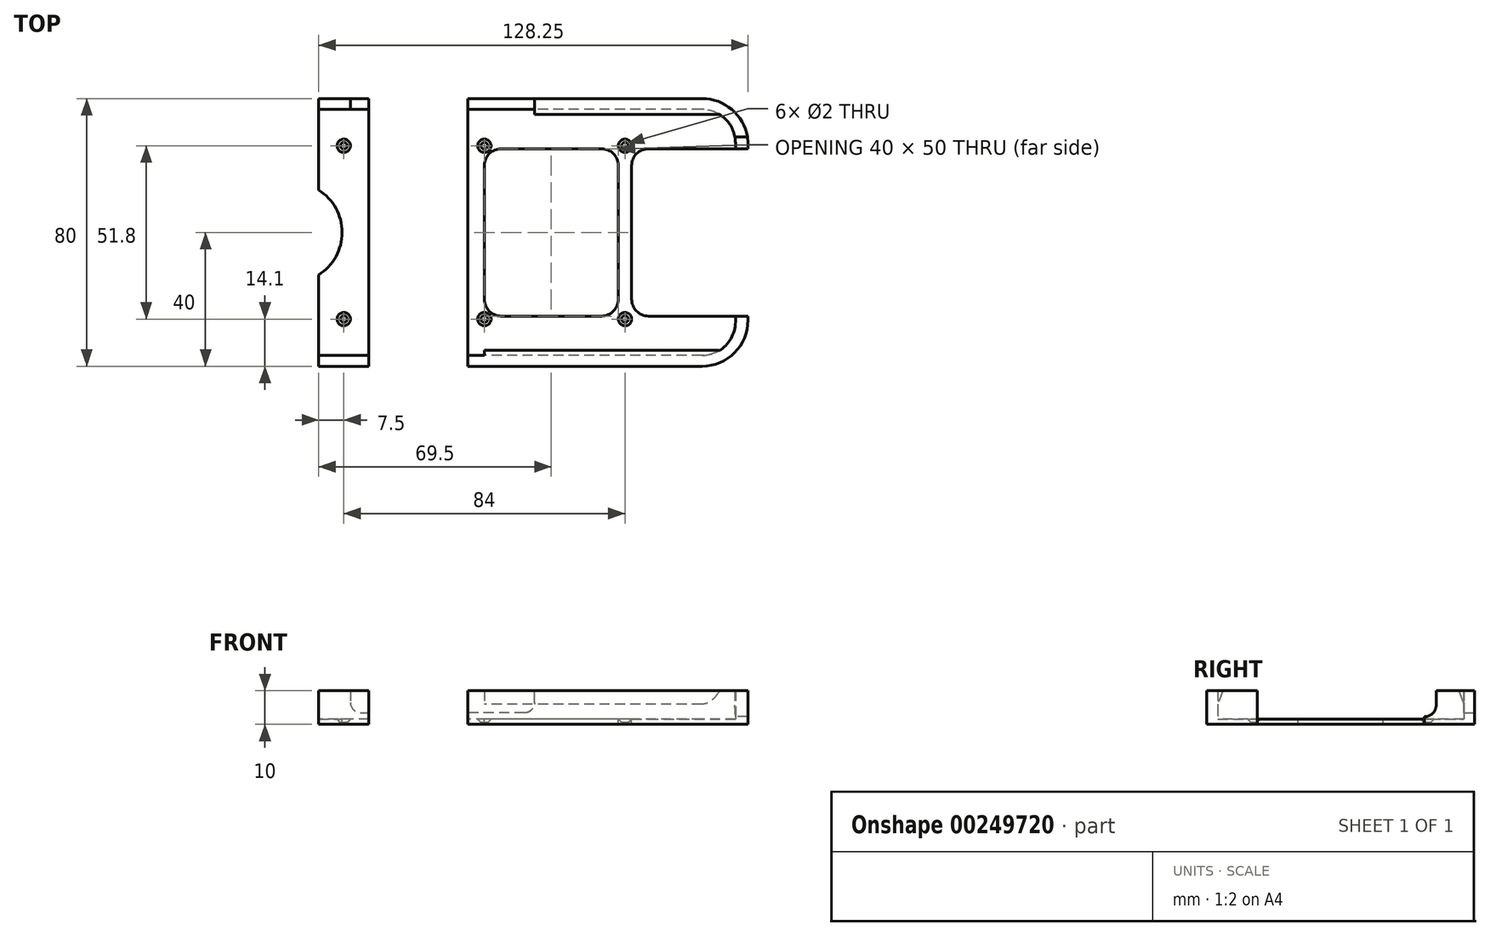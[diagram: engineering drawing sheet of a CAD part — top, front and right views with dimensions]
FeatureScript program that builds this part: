
annotation { "Feature Type Name" : "Feature", "Feature Type Description" : "" }
export const myFeature = defineFeature(function(context is Context, id is Id, definition is map)
    precondition{}
    {
        {
            var Q0;
            Q0=qCreatedBy(makeId("Top.planeOp"),FACE);
            var sketch = newSketch(context, id + "F0", { "sketchPlane" : qUnion([Q0])});
            skCircle(sketch, "E0", {"center": v(0, 25.9) * mm, "radius": 1 * mm});
            skCircle(sketch, "E1", {"center": v(0, -25.9) * mm, "radius": 1 * mm});
            skLineSegment(sketch, "E2", {"start": v(0, 25.9) * mm, "end": v(0, -25.9) * mm, "construction": true});
            skCircle(sketch, "E3", {"center": v(-42, 25.9) * mm, "radius": 1 * mm});
            skCircle(sketch, "E4", {"center": v(42, 25.9) * mm, "radius": 1 * mm});
            skLineSegment(sketch, "E5", {"start": v(-42, 25.9) * mm, "end": v(42, 25.9) * mm, "construction": true});
            skCircle(sketch, "E6.MirrorC", {"center": v(-42, -25.9) * mm, "radius": 1 * mm});
            skCircle(sketch, "E7.MirrorC", {"center": v(42, -25.9) * mm, "radius": 1 * mm});
            skLineSegment(sketch, "E8", {"start": v(75, 26.75) * mm, "end": v(75, -26.75) * mm});
            skPoint(sketch, "E9.middle", {"position": v(0, 0) * mm});
            skPoint(sketch, "E10", {"position": v(75, 0) * mm});
            skLineSegment(sketch, "E11", {"start": v(65, 36.75) * mm, "end": v(0, 36.75) * mm});
            skLineSegment(sketch, "E12", {"start": v(65, -36.75) * mm, "end": v(0, -36.75) * mm});
            skPoint(sketch, "E13.visualSharp", {"position": v(75, 36.75) * mm});
            skArc(sketch, "E13.filletArc", {"start": v(75, 26.75) * mm, "mid": v(72.07, 33.82) * mm, "end": v(65, 36.75) * mm});
            skPoint(sketch, "E14.visualSharp", {"position": v(75, -36.75) * mm});
            skArc(sketch, "E14.filletArc", {"start": v(65, -36.75) * mm, "mid": v(72.07, -33.82) * mm, "end": v(75, -26.75) * mm});
            skLineSegment(sketch, "E15", {"start": v(-5, 40) * mm, "end": v(-5, -40) * mm});
            skPoint(sketch, "E16", {"position": v(-5, 0) * mm});
            skLineSegment(sketch, "E17", {"start": v(0, 36.75) * mm, "end": v(-5, 36.75) * mm});
            skLineSegment(sketch, "E18", {"start": v(0, -36.75) * mm, "end": v(-5, -36.75) * mm});
            skLineSegment(sketch, "E19", {"start": v(-5, 40) * mm, "end": v(65, 40) * mm});
            skLineSegment(sketch, "E20", {"start": v(-5, -40) * mm, "end": v(65, -40) * mm});
            skLineSegment(sketch, "E21", {"start": v(78.75, 26.25) * mm, "end": v(78.75, -26.25) * mm});
            skPoint(sketch, "E22.visualSharp", {"position": v(78.75, 40) * mm});
            skArc(sketch, "E22.filletArc", {"start": v(78.75, 26.25) * mm, "mid": v(74.72, 35.97) * mm, "end": v(65, 40) * mm});
            skPoint(sketch, "E23.visualSharp", {"position": v(78.75, -40) * mm});
            skArc(sketch, "E23.filletArc", {"start": v(65, -40) * mm, "mid": v(74.72, -35.97) * mm, "end": v(78.75, -26.25) * mm});
            skLineSegment(sketch, "E24", {"start": v(25, 36.75) * mm, "end": v(25, 40) * mm});
            skLineSegment(sketch, "E25.MirrorCS", {"start": v(25, -36.75) * mm, "end": v(25, -40) * mm});
            skLineSegment(sketch, "E26", {"start": v(75, 25) * mm, "end": v(78.75, 25) * mm});
            skLineSegment(sketch, "E27", {"start": v(75, -25) * mm, "end": v(78.75, -25) * mm});
            skLineSegment(sketch, "E28", {"start": v(-42, 25.9) * mm, "end": v(-42, -25.9) * mm, "construction": true});
            skLineSegment(sketch, "E29.bottom", {"start": v(-34.5, -40) * mm, "end": v(-49.5, -40) * mm});
            skLineSegment(sketch, "E29.top", {"start": v(-34.5, 40) * mm, "end": v(-49.5, 40) * mm});
            skLineSegment(sketch, "E29.left", {"start": v(-34.5, -40) * mm, "end": v(-34.5, 40) * mm});
            skLineSegment(sketch, "E29.right", {"start": v(-49.5, -40) * mm, "end": v(-49.5, 40) * mm});
            skPoint(sketch, "E29.middle", {"position": v(-42, 0) * mm});
            skLineSegment(sketch, "E30", {"start": v(-34.5, 36.75) * mm, "end": v(-49.5, 36.75) * mm});
            skLineSegment(sketch, "E31", {"start": v(-34.5, -36.75) * mm, "end": v(-49.5, -36.75) * mm});
            skArc(sketch, "E32", {"start": v(-49.5, 12.69) * mm, "mid": v(-42.5, 0) * mm, "end": v(-49.5, -12.69) * mm});
            skLineSegment(sketch, "E33", {"start": v(75, 25) * mm, "end": v(49, 25) * mm});
            skLineSegment(sketch, "E34", {"start": v(44, 20) * mm, "end": v(44, -20) * mm});
            skLineSegment(sketch, "E35", {"start": v(49, -25) * mm, "end": v(75, -25) * mm});
            skPoint(sketch, "E36", {"position": v(44, 0) * mm});
            skLineSegment(sketch, "E37.bottom", {"start": v(35, -25) * mm, "end": v(5, -25) * mm});
            skLineSegment(sketch, "E37.top", {"start": v(35, 25) * mm, "end": v(5, 25) * mm});
            skLineSegment(sketch, "E37.left", {"start": v(40, -20) * mm, "end": v(40, 20) * mm});
            skLineSegment(sketch, "E37.right", {"start": v(0, -20) * mm, "end": v(0, 20) * mm});
            skPoint(sketch, "E37.middle", {"position": v(20, 0) * mm});
            skPoint(sketch, "E38.visualSharp", {"position": v(0, 25) * mm});
            skArc(sketch, "E38.filletArc", {"start": v(5, 25) * mm, "mid": v(1.46, 23.54) * mm, "end": v(0, 20) * mm});
            skPoint(sketch, "E39.visualSharp", {"position": v(40, 25) * mm});
            skArc(sketch, "E39.filletArc", {"start": v(40, 20) * mm, "mid": v(38.54, 23.54) * mm, "end": v(35, 25) * mm});
            skPoint(sketch, "E40.visualSharp", {"position": v(44, 25) * mm});
            skArc(sketch, "E40.filletArc", {"start": v(49, 25) * mm, "mid": v(45.46, 23.54) * mm, "end": v(44, 20) * mm});
            skPoint(sketch, "E41.visualSharp", {"position": v(0, -25) * mm});
            skArc(sketch, "E41.filletArc", {"start": v(0, -20) * mm, "mid": v(1.46, -23.54) * mm, "end": v(5, -25) * mm});
            skPoint(sketch, "E42.visualSharp", {"position": v(40, -25) * mm});
            skArc(sketch, "E42.filletArc", {"start": v(35, -25) * mm, "mid": v(38.54, -23.54) * mm, "end": v(40, -20) * mm});
            skPoint(sketch, "E43.visualSharp", {"position": v(44, -25) * mm});
            skArc(sketch, "E43.filletArc", {"start": v(44, -20) * mm, "mid": v(45.46, -23.54) * mm, "end": v(49, -25) * mm});
            skSolve(sketch);
        }
        {
            var Q0;
            Q0=makeQuery(id+"F0.imprint","IMPRINT",FACE,{"disambiguationData":[TD([[makeQuery(id+"F0.imprint","IMPRINT",EDGE,{"derivedFrom":sQuery(id+"F0.wireOp",EDGE,"E0")}),-1.0]])]});
            var Q1;
            Q1=makeQuery(id+"F0.imprint","IMPRINT",FACE,{"disambiguationData":[TD([[makeQuery(id+"F0.imprint","IMPRINT",EDGE,{"derivedFrom":sQuery(id+"F0.wireOp",EDGE,"E3")}),-1.0]])]});
            var Q2;
            {var subQ0=sQuery(id+"F0.wireOp",EDGE,"E29.top");Q2=makeQuery(id+"F0.imprint","IMPRINT",FACE,{"disambiguationData":[TD([[makeQuery(id+"F0.imprint","IMPRINT",EDGE,{"derivedFrom":subQ0}),1.0]])]});}
            var Q3;
            {var subQ4=sQuery(id+"F0.wireOp",EDGE,"E17");Q3=makeQuery(id+"F0.imprint","IMPRINT",FACE,{"disambiguationData":[TD([[makeQuery(id+"F0.imprint","IMPRINT",EDGE,{"derivedFrom":subQ4}),-1.0]])]});}
            var Q4;
            {var subQ0=sQuery(id+"F0.wireOp",EDGE,"E29.bottom");Q4=makeQuery(id+"F0.imprint","IMPRINT",FACE,{"disambiguationData":[TD([[makeQuery(id+"F0.imprint","IMPRINT",EDGE,{"derivedFrom":subQ0}),-1.0]])]});}
            var Q5;
            {var subQ4=sQuery(id+"F0.wireOp",EDGE,"E18");Q5=makeQuery(id+"F0.imprint","IMPRINT",FACE,{"disambiguationData":[TD([[makeQuery(id+"F0.imprint","IMPRINT",EDGE,{"derivedFrom":subQ4}),1.0]])]});}
            var Q6;
            {var subQ3=sQuery(id+"F0.wireOp",EDGE,"E14.filletArc");Q6=makeQuery(id+"F0.imprint","IMPRINT",FACE,{"disambiguationData":[TD([[makeQuery(id+"F0.imprint","IMPRINT",EDGE,{"derivedFrom":subQ3}),-1.0]])]});}
            var Q7;
            {var subQ0=sQuery(id+"F0.wireOp",EDGE,"E13.filletArc");Q7=makeQuery(id+"F0.imprint","IMPRINT",FACE,{"disambiguationData":[TD([[makeQuery(id+"F0.imprint","IMPRINT",EDGE,{"derivedFrom":subQ0}),-1.0]])]});}
            extrude(context, id + "F1", {"entities" : qUnion([Q0, Q1, Q2, Q3, Q4, Q5, Q6, Q7]), "oppositeDirection" : true, "depth" : 1.5 * mm});
        }
        {
            var Q0;
            {var subQ0=sQuery(id+"F0.wireOp",EDGE,"E13.filletArc");Q0=makeQuery(id+"F0.imprint","IMPRINT",FACE,{"disambiguationData":[TD([[makeQuery(id+"F0.imprint","IMPRINT",EDGE,{"derivedFrom":subQ0}),-1.0]])]});}
            var Q1;
            {var subQ3=sQuery(id+"F0.wireOp",EDGE,"E14.filletArc");Q1=makeQuery(id+"F0.imprint","IMPRINT",FACE,{"disambiguationData":[TD([[makeQuery(id+"F0.imprint","IMPRINT",EDGE,{"derivedFrom":subQ3}),-1.0]])]});}
            var Q2;
            {var subQ4=sQuery(id+"F0.wireOp",EDGE,"E18");Q2=makeQuery(id+"F0.imprint","IMPRINT",FACE,{"disambiguationData":[TD([[makeQuery(id+"F0.imprint","IMPRINT",EDGE,{"derivedFrom":subQ4}),1.0]])]});}
            var Q3;
            {var subQ0=sQuery(id+"F0.wireOp",EDGE,"E29.bottom");Q3=makeQuery(id+"F0.imprint","IMPRINT",FACE,{"disambiguationData":[TD([[makeQuery(id+"F0.imprint","IMPRINT",EDGE,{"derivedFrom":subQ0}),-1.0]])]});}
            var Q4;
            {var subQ4=sQuery(id+"F0.wireOp",EDGE,"E17");Q4=makeQuery(id+"F0.imprint","IMPRINT",FACE,{"disambiguationData":[TD([[makeQuery(id+"F0.imprint","IMPRINT",EDGE,{"derivedFrom":subQ4}),-1.0]])]});}
            var Q5;
            {var subQ0=sQuery(id+"F0.wireOp",EDGE,"E29.top");Q5=makeQuery(id+"F0.imprint","IMPRINT",FACE,{"disambiguationData":[TD([[makeQuery(id+"F0.imprint","IMPRINT",EDGE,{"derivedFrom":subQ0}),1.0]])]});}
            extrude(context, id + "F2", {"entities" : qUnion([Q0, Q1, Q2, Q3, Q4, Q5]), "operationType" : NewBodyOperationType.ADD, "depth" : 8.5 * mm});
        }
        {
            var Q0;
            Q0=qCreatedBy(makeId("Right.planeOp"),FACE);
            var sketch = newSketch(context, id + "F3", { "sketchPlane" : qUnion([Q0])});
            skPoint(sketch, "E44", {"position": v(36.75, 4.5) * mm});
            skLineSegment(sketch, "E45", {"start": v(36.75, 8.5) * mm, "end": v(36.75, 4.5) * mm});
            skLineSegment(sketch, "E46", {"start": v(36.75, 8.5) * mm, "end": v(35.25, 8.5) * mm});
            skLineSegment(sketch, "E47", {"start": v(35.25, 8.5) * mm, "end": v(36.75, 4.5) * mm});
            skPoint(sketch, "E48.MirrorP", {"position": v(-36.75, 4.5) * mm});
            skLineSegment(sketch, "E49.MirrorCS", {"start": v(-36.75, 8.5) * mm, "end": v(-36.75, 4.5) * mm});
            skLineSegment(sketch, "E50.MirrorCS", {"start": v(-36.75, 8.5) * mm, "end": v(-35.25, 8.5) * mm});
            skLineSegment(sketch, "E51.MirrorCS", {"start": v(-35.25, 8.5) * mm, "end": v(-36.75, 4.5) * mm});
            skPoint(sketch, "E52.0", {"position": v(36.75, 8.5) * mm});
            skSolve(sketch);
        }
        {
            var Q0;
            Q0=makeQuery(id+"F3.imprint","IMPRINT",FACE,{"disambiguationData":[TD([[makeQuery(id+"F3.imprint","IMPRINT",EDGE,{"derivedFrom":sQuery(id+"F3.wireOp",EDGE,"E45")}),-1.0]])]});
            var Q1;
            Q1=makeQuery(id+"F3.imprint","IMPRINT",FACE,{"disambiguationData":[TD([[makeQuery(id+"F3.imprint","IMPRINT",EDGE,{"derivedFrom":sQuery(id+"F3.wireOp",EDGE,"E49.MirrorCS")}),1.0]])]});
            extrude(context, id + "F4", {"entities" : qUnion([Q0, Q1]), "operationType" : NewBodyOperationType.ADD, "depth" : 70 * mm});
        }
        {
            var Q0;
            Q0=qCreatedBy(makeId("Right.planeOp"),FACE);
            var sketch = newSketch(context, id + "F5", { "sketchPlane" : qUnion([Q0])});
            skPoint(sketch, "E53.0", {"position": v(25, 8.5) * mm});
            skPoint(sketch, "E54.0", {"position": v(25, 4.25) * mm});
            skArc(sketch, "E55", {"start": v(25, 7.75) * mm, "mid": v(28.5, 4.25) * mm, "end": v(25, 0.75) * mm});
            skLineSegment(sketch, "E56", {"start": v(25, 7.75) * mm, "end": v(25, 0.75) * mm});
            skLineSegment(sketch, "E57", {"start": v(25, 7.75) * mm, "end": v(25, 8.5) * mm});
            skLineSegment(sketch, "E58", {"start": v(28.5, 8.5) * mm, "end": v(28.5, 4.25) * mm});
            skPoint(sketch, "E58.startSnap0", {"position": v(28.5, 4.25) * mm});
            skLineSegment(sketch, "E59", {"start": v(28.5, 8.5) * mm, "end": v(25, 8.5) * mm});
            skSolve(sketch);
        }
        {
            var Q0;
            {var subQ0=sQuery(id+"F5.wireOp",EDGE,"E56");Q0=makeQuery(id+"F5.imprint","IMPRINT",FACE,{"disambiguationData":[TD([[makeQuery(id+"F5.imprint","IMPRINT",EDGE,{"derivedFrom":subQ0}),1.0]])]});}
            var Q1;
            {var subQ0=sQuery(id+"F5.wireOp",EDGE,"E57");Q1=makeQuery(id+"F5.imprint","IMPRINT",FACE,{"disambiguationData":[TD([[makeQuery(id+"F5.imprint","IMPRINT",EDGE,{"derivedFrom":subQ0}),-1.0]])]});}
            extrude(context, id + "F6", {"entities" : qUnion([Q0, Q1]), "operationType" : NewBodyOperationType.REMOVE, "endBound" : BoundingType.THROUGH_ALL, "depth" : 25 * mm});
        }
        {
            var Q0;
            Q0=qCreatedBy(makeId("Front.planeOp"),FACE);
            var sketch = newSketch(context, id + "F7", { "sketchPlane" : qUnion([Q0])});
            skPoint(sketch, "E60.0", {"position": v(75, 0) * mm});
            skLineSegment(sketch, "E61.bottom", {"start": v(12, 2) * mm, "end": v(-37, 2) * mm});
            skLineSegment(sketch, "E61.top", {"start": v(15, 12) * mm, "end": v(-40, 12) * mm});
            skLineSegment(sketch, "E61.left", {"start": v(15, 5) * mm, "end": v(15, 12) * mm});
            skLineSegment(sketch, "E61.right", {"start": v(-40, 5) * mm, "end": v(-40, 12) * mm});
            skPoint(sketch, "E62.visualSharp", {"position": v(-40, 2) * mm});
            skArc(sketch, "E62.filletArc", {"start": v(-40, 5) * mm, "mid": v(-39.12, 2.88) * mm, "end": v(-37, 2) * mm});
            skPoint(sketch, "E63.visualSharp", {"position": v(15, 2) * mm});
            skArc(sketch, "E63.filletArc", {"start": v(12, 2) * mm, "mid": v(14.12, 2.88) * mm, "end": v(15, 5) * mm});
            skSolve(sketch);
        }
        {
            var Q0;
            Q0=makeQuery(id+"F7.imprint","IMPRINT",FACE,{"disambiguationData":[TD([[makeQuery(id+"F7.imprint","IMPRINT",EDGE,{"derivedFrom":sQuery(id+"F7.wireOp",EDGE,"E61.bottom")}),-1.0]])]});
            extrude(context, id + "F8", {"entities" : qUnion([Q0]), "operationType" : NewBodyOperationType.REMOVE, "oppositeDirection" : true, "depth" : 50 * mm});
        }
        {
            var Q0;
            Q0=makeQuery(id+"F1.opExtrude","CAP_EDGE",EDGE,{"disambiguationData":[OSD([sQuery(id+"F0.wireOp",EDGE,"E3")])],"isStart":true});
            var Q1;
            Q1=makeQuery(id+"F1.opExtrude","CAP_EDGE",EDGE,{"disambiguationData":[OSD([sQuery(id+"F0.wireOp",EDGE,"E6.MirrorC")])],"isStart":true});
            var Q2;
            Q2=makeQuery(id+"F1.opExtrude","CAP_EDGE",EDGE,{"disambiguationData":[OSD([sQuery(id+"F0.wireOp",EDGE,"E0")])],"isStart":true});
            var Q3;
            Q3=makeQuery(id+"F1.opExtrude","CAP_EDGE",EDGE,{"disambiguationData":[OSD([sQuery(id+"F0.wireOp",EDGE,"E1")])],"isStart":true});
            var Q4;
            Q4=makeQuery(id+"F1.opExtrude","CAP_EDGE",EDGE,{"disambiguationData":[OSD([sQuery(id+"F0.wireOp",EDGE,"E4")])],"isStart":true});
            var Q5;
            Q5=makeQuery(id+"F1.opExtrude","CAP_EDGE",EDGE,{"disambiguationData":[OSD([sQuery(id+"F0.wireOp",EDGE,"E7.MirrorC")])],"isStart":true});
            chamfer(context, id + "F9", {"entities" : qUnion([Q0, Q1, Q2, Q3, Q4, Q5]), "width" : 1 * mm, "tangentPropagation" : true});
        }
    });
